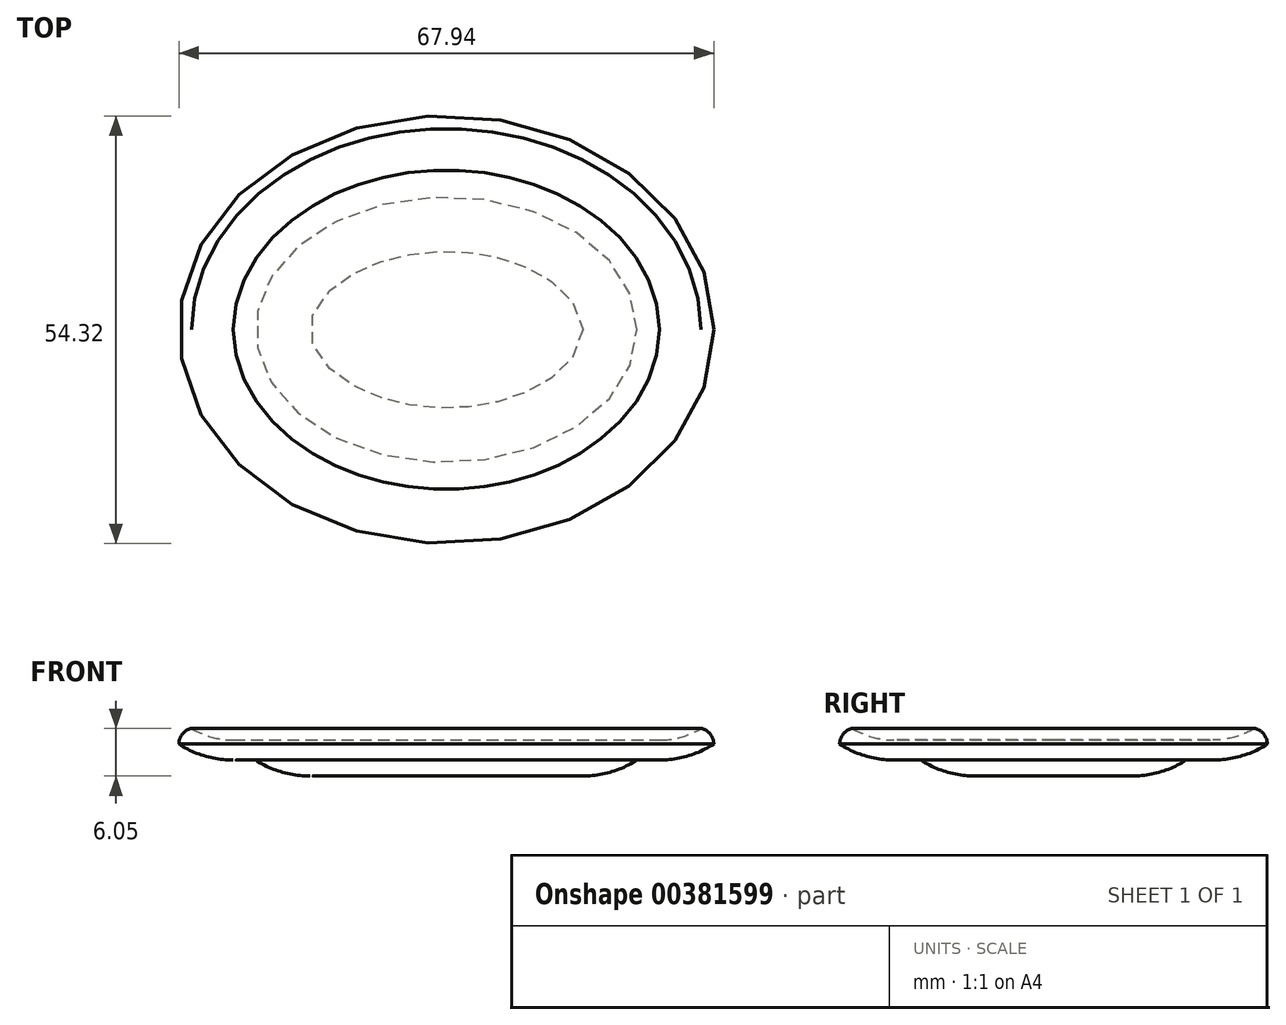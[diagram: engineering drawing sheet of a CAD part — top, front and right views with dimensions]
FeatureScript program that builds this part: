
annotation { "Feature Type Name" : "Feature", "Feature Type Description" : "" }
export const myFeature = defineFeature(function(context is Context, id is Id, definition is map)
    precondition{}
    {
        {
            var Q0;
            Q0=qCreatedBy(makeId("Top.planeOp"),FACE);
            var sketch = newSketch(context, id + "F0", { "sketchPlane" : qUnion([Q0])});
            skEllipse(sketch, "E0", {"center": v(0, 0) * mm, "majorRadius": 33.97 * mm, "minorRadius": 27.16 * mm, "majorAxis": v(1, 0)});
            skSolve(sketch);
        }
        {
            var Q0;
            Q0=qCreatedBy(makeId("Top.planeOp"),FACE);
            var sketch = newSketch(context, id + "F1", { "sketchPlane" : qUnion([Q0])});
            skEllipse(sketch, "E1", {"center": v(0, 0) * mm, "majorRadius": 24.22 * mm, "minorRadius": 16.84 * mm, "majorAxis": v(1, 0)});
            skSolve(sketch);
        }
        {
            var Q0;
            Q0=makeQuery(id+"F1.imprint","IMPRINT",FACE,{"disambiguationData":[TD([[makeQuery(id+"F1.imprint","IMPRINT",EDGE,{"derivedFrom":sQuery(id+"F1.wireOp",EDGE,"E1")}),1.0]])]});
            extrude(context, id + "F2", {"entities" : qUnion([Q0]), "oppositeDirection" : true, "depth" : 2.03 * mm});
        }
        {
            var Q0;
            Q0=makeQuery(id+"F0.imprint","IMPRINT",FACE,{"disambiguationData":[TD([[makeQuery(id+"F0.imprint","IMPRINT",EDGE,{"derivedFrom":sQuery(id+"F0.wireOp",EDGE,"E0")}),1.0]])]});
            extrude(context, id + "F3", {"entities" : qUnion([Q0]), "operationType" : NewBodyOperationType.ADD, "depth" : 2.03 * mm});
        }
        {
            var Q0;
            Q0=makeQuery(id+"F2.opExtrude","CAP_EDGE",EDGE,{"disambiguationData":[OSD([sQuery(id+"F1.wireOp",EDGE,"E1")])],"isStart":false});
            fillet(context, id + "F4", {"entities" : qUnion([Q0]), "radius" : 12.7 * mm, "tangentPropagation" : true, "allowEdgeOverflow" : false});
        }
        {
            var Q0;
            Q0=makeQuery(id+"F3.opExtrude","CAP_EDGE",EDGE,{"disambiguationData":[OSD([sQuery(id+"F0.wireOp",EDGE,"E0")])],"isStart":true});
            fillet(context, id + "F5", {"entities" : qUnion([Q0]), "radius" : 12.7 * mm, "tangentPropagation" : true, "allowEdgeOverflow" : false});
        }
        {
            var Q0;
            Q0=makeQuery(id+"F3.opExtrude","CAP_FACE",FACE,{"disambiguationData":[OSD([sQuery(id+"F0.wireOp",EDGE,"E0")])],"isStart":false});
            extrude(context, id + "F6", {"entities" : qUnion([Q0]), "operationType" : NewBodyOperationType.ADD, "depth" : 2.03 * mm});
        }
        {
            var Q0;
            Q0=makeQuery(id+"F6.opExtrude","CAP_EDGE",EDGE,{"disambiguationData":[OSD([sQuery(id+"F0.wireOp",EDGE,"E0")])],"isStart":false});
            fillet(context, id + "F7", {"entities" : qUnion([Q0]), "radius" : 2.03 * mm, "tangentPropagation" : true, "allowEdgeOverflow" : false});
        }
        {
            var Q0;
            Q0=makeQuery(id+"F6.opExtrude","CAP_FACE",FACE,{"disambiguationData":[OSD([sQuery(id+"F0.wireOp",EDGE,"E0")])],"isStart":false});
            var Q1;
            Q1=makeQuery(id+"F7.opFillet","BLEND_FACE",FACE,{"disambiguationData":[OSD([sQuery(id+"F0.wireOp",EDGE,"E0")])]});
            shell(context, id + "F8", {"entities" : qUnion([Q0, Q1]), "thickness" : 2.54 * mm});
        }
    });
